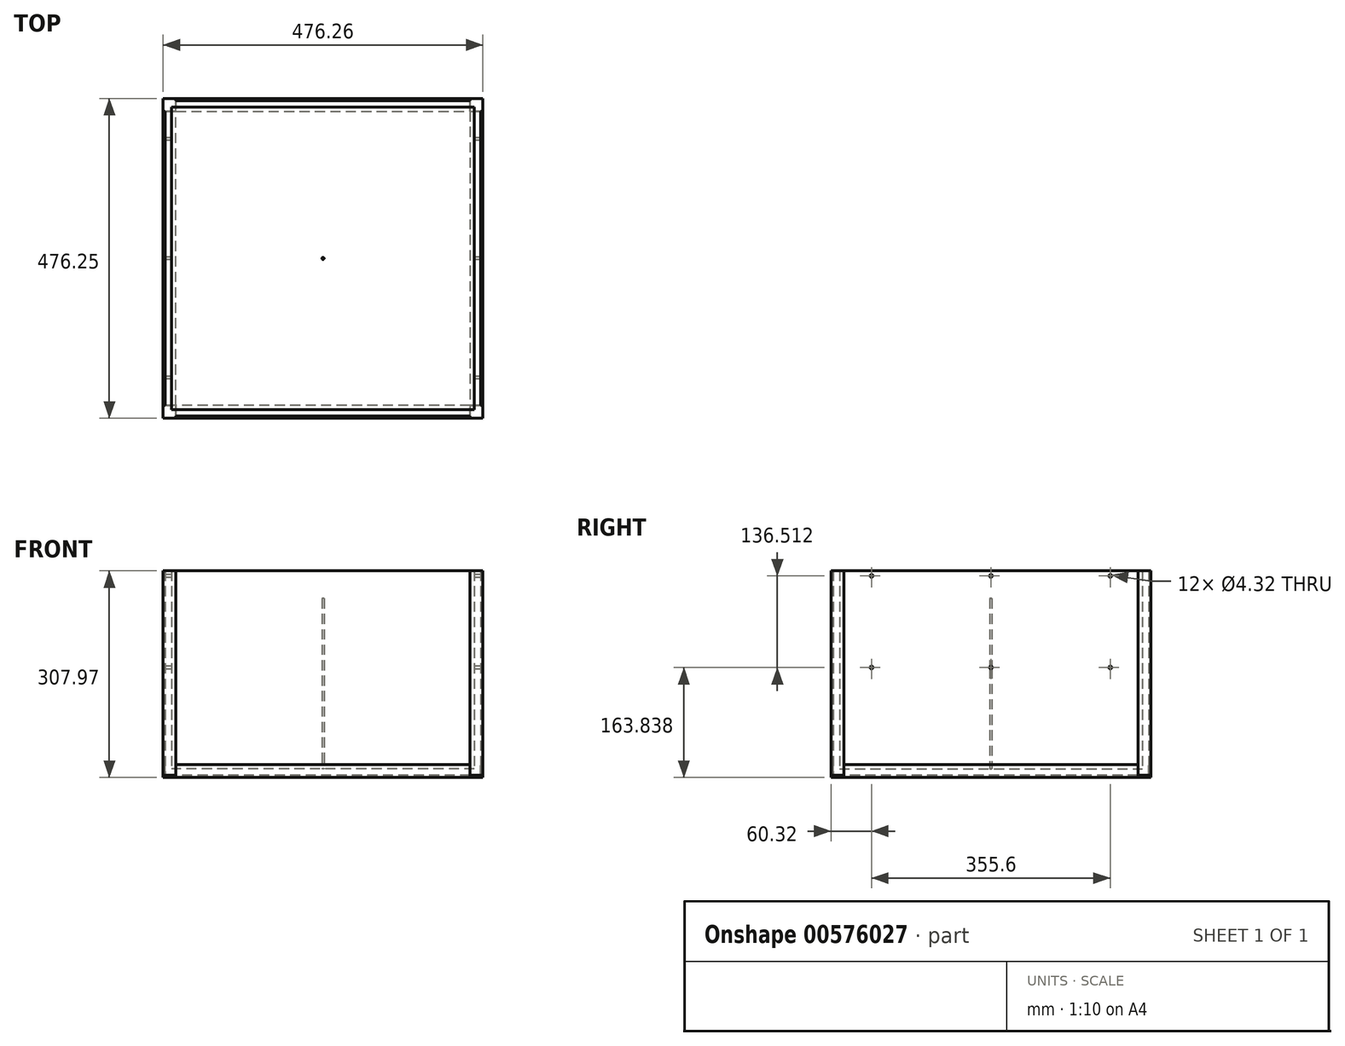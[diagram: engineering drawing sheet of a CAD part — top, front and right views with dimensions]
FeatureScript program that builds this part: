
annotation { "Feature Type Name" : "Feature", "Feature Type Description" : "" }
export const myFeature = defineFeature(function(context is Context, id is Id, definition is map)
    precondition{}
    {
        {
            var Q0;
            Q0=qCreatedBy(makeId("Top.planeOp"),FACE);
            var sketch = newSketch(context, id + "F0", { "sketchPlane" : qUnion([Q0])});
            skLineSegment(sketch, "E0.bottom", {"start": v(234.95, -234.95) * mm, "end": v(-234.95, -234.95) * mm});
            skLineSegment(sketch, "E0.top", {"start": v(234.95, 234.95) * mm, "end": v(-234.95, 234.95) * mm});
            skLineSegment(sketch, "E0.left", {"start": v(234.95, -234.95) * mm, "end": v(234.95, 234.95) * mm});
            skLineSegment(sketch, "E0.right", {"start": v(-234.95, -234.95) * mm, "end": v(-234.95, 234.95) * mm});
            skPoint(sketch, "E0.middle", {"position": v(0, 0) * mm});
            skLineSegment(sketch, "E1", {"start": v(-234.95, 238.13) * mm, "end": v(-238.13, 238.13) * mm});
            skLineSegment(sketch, "E2", {"start": v(-238.13, 238.13) * mm, "end": v(-238.13, 219.08) * mm});
            skLineSegment(sketch, "E3", {"start": v(-238.13, 219.08) * mm, "end": v(-234.95, 219.08) * mm});
            skLineSegment(sketch, "E4", {"start": v(-238.13, 238.13) * mm, "end": v(-219.08, 238.13) * mm});
            skLineSegment(sketch, "E5", {"start": v(-219.08, 238.13) * mm, "end": v(-219.08, 234.95) * mm});
            skLineSegment(sketch, "E6.1.0", {"start": v(-238.13, -238.13) * mm, "end": v(-238.13, -219.08) * mm});
            skLineSegment(sketch, "E6.1.1", {"start": v(-238.13, -238.13) * mm, "end": v(-219.08, -238.13) * mm});
            skLineSegment(sketch, "E6.1.2", {"start": v(-219.08, -238.13) * mm, "end": v(-219.08, -234.95) * mm});
            skLineSegment(sketch, "E6.1.3", {"start": v(-238.13, -219.08) * mm, "end": v(-234.95, -219.08) * mm});
            skLineSegment(sketch, "E6.1.4", {"start": v(-238.13, -234.95) * mm, "end": v(-238.13, -238.13) * mm});
            skLineSegment(sketch, "E6.2.0", {"start": v(238.13, -238.13) * mm, "end": v(219.08, -238.13) * mm});
            skLineSegment(sketch, "E6.2.1", {"start": v(238.13, -238.13) * mm, "end": v(238.13, -219.08) * mm});
            skLineSegment(sketch, "E6.2.2", {"start": v(238.13, -219.08) * mm, "end": v(234.95, -219.08) * mm});
            skLineSegment(sketch, "E6.2.3", {"start": v(219.08, -238.13) * mm, "end": v(219.08, -234.95) * mm});
            skLineSegment(sketch, "E6.2.4", {"start": v(234.95, -238.13) * mm, "end": v(238.13, -238.13) * mm});
            skLineSegment(sketch, "E6.3.0", {"start": v(238.13, 238.13) * mm, "end": v(238.13, 219.08) * mm});
            skLineSegment(sketch, "E6.3.1", {"start": v(238.13, 238.13) * mm, "end": v(219.08, 238.13) * mm});
            skLineSegment(sketch, "E6.3.2", {"start": v(219.08, 238.13) * mm, "end": v(219.08, 234.95) * mm});
            skLineSegment(sketch, "E6.3.3", {"start": v(238.13, 219.08) * mm, "end": v(234.95, 219.08) * mm});
            skLineSegment(sketch, "E6.3.4", {"start": v(238.13, 234.95) * mm, "end": v(238.13, 238.13) * mm});
            skLineSegment(sketch, "E7.0", {"start": v(225.43, 225.43) * mm, "end": v(-225.42, 225.42) * mm});
            skLineSegment(sketch, "E7.1", {"start": v(225.43, -225.42) * mm, "end": v(225.43, 225.42) * mm});
            skLineSegment(sketch, "E7.2", {"start": v(225.43, -225.42) * mm, "end": v(-225.43, -225.43) * mm});
            skLineSegment(sketch, "E7.3", {"start": v(-225.43, -225.43) * mm, "end": v(-225.42, 225.42) * mm});
            skSolve(sketch);
        }
        {
            var Q0;
            Q0 = qSketchRegion(id + "F0", true);
            extrude(context, id + "F1", {"entities" : qUnion([Q0]), "depth" : 304.8 * mm, "offsetDistance" : 25.4 * mm});
        }
        {
            var Q0;
            Q0=makeQuery(id+"F0.imprint","IMPRINT",FACE,{"disambiguationData":[TD([[makeQuery(id+"F0.imprint","IMPRINT",EDGE,{"derivedFrom":sQuery(id+"F0.wireOp",EDGE,"E7.0")}),1.0]])]});
            extrude(context, id + "F2", {"entities" : qUnion([Q0]), "operationType" : NewBodyOperationType.ADD, "depth" : 9.52 * mm, "offsetDistance" : 25.4 * mm});
        }
        {
            var Q0;
            Q0=makeQuery(id+"F1.opExtrude","SWEPT_FACE",FACE,{"disambiguationData":[OSD([sQuery(id+"F0.wireOp",EDGE,"E0.right")])]});
            var sketch = newSketch(context, id + "F3", { "sketchPlane" : qUnion([Q0])});
            skLineSegment(sketch, "E8", {"start": v(0, 304.8) * mm, "end": v(0, 297.18) * mm});
            skLineSegment(sketch, "E9", {"start": v(0, 304.8) * mm, "end": v(-177.8, 304.8) * mm});
            skLineSegment(sketch, "E10", {"start": v(-177.8, 304.8) * mm, "end": v(-177.8, 297.18) * mm});
            skLineSegment(sketch, "E11", {"start": v(0, 297.18) * mm, "end": v(0, 160.67) * mm});
            skLineSegment(sketch, "E12", {"start": v(-177.8, 297.18) * mm, "end": v(-177.8, 160.67) * mm});
            skLineSegment(sketch, "E13.MirrorCS", {"start": v(177.8, 304.8) * mm, "end": v(177.8, 297.18) * mm});
            skLineSegment(sketch, "E14.MirrorCS", {"start": v(177.8, 297.18) * mm, "end": v(177.8, 160.67) * mm});
            skLineSegment(sketch, "E15.MirrorCS", {"start": v(0, 304.8) * mm, "end": v(177.8, 304.8) * mm});
            skSolve(sketch);
        }
        {
            var Q0;
            Q0=sQuery(id+"F3.wireOp",VERTEX,"E12.start");
            var Q1;
            Q1=sQuery(id+"F3.wireOp",VERTEX,"E12.end");
            var Q2;
            Q2=sQuery(id+"F3.wireOp",VERTEX,"E8.end");
            var Q3;
            Q3=sQuery(id+"F3.wireOp",VERTEX,"E11.end");
            var Q4;
            Q4=sQuery(id+"F3.wireOp",VERTEX,"E14.MirrorCS.start");
            var Q5;
            Q5=sQuery(id+"F3.wireOp",VERTEX,"E14.MirrorCS.end");
            var Q6;
            Q6=makeQuery(id+"F1.opExtrude","SWEPT_BODY",BODY,{"disambiguationData":[OSD([sQuery(id+"F0.wireOp",EDGE,"E0.bottom"),sQuery(id+"F0.wireOp",EDGE,"E0.top"),sQuery(id+"F0.wireOp",EDGE,"E0.left"),sQuery(id+"F0.wireOp",EDGE,"E0.right"),sQuery(id+"F0.wireOp",EDGE,"E2"),sQuery(id+"F0.wireOp",EDGE,"E3"),sQuery(id+"F0.wireOp",EDGE,"E4"),sQuery(id+"F0.wireOp",EDGE,"E5"),sQuery(id+"F0.wireOp",EDGE,"E6.1.0"),sQuery(id+"F0.wireOp",EDGE,"E6.1.1"),sQuery(id+"F0.wireOp",EDGE,"E6.1.2"),sQuery(id+"F0.wireOp",EDGE,"E6.1.3"),sQuery(id+"F0.wireOp",EDGE,"E6.1.4"),sQuery(id+"F0.wireOp",EDGE,"E6.2.0"),sQuery(id+"F0.wireOp",EDGE,"E6.2.1"),sQuery(id+"F0.wireOp",EDGE,"E6.2.2"),sQuery(id+"F0.wireOp",EDGE,"E6.2.3"),sQuery(id+"F0.wireOp",EDGE,"E6.2.4"),sQuery(id+"F0.wireOp",EDGE,"E6.3.0"),sQuery(id+"F0.wireOp",EDGE,"E6.3.1"),sQuery(id+"F0.wireOp",EDGE,"E6.3.2"),sQuery(id+"F0.wireOp",EDGE,"E6.3.3"),sQuery(id+"F0.wireOp",EDGE,"E6.3.4"),sQuery(id+"F0.wireOp",EDGE,"E7.0"),sQuery(id+"F0.wireOp",EDGE,"E7.1"),sQuery(id+"F0.wireOp",EDGE,"E7.2"),sQuery(id+"F0.wireOp",EDGE,"E7.3")])]});
            hole(context, id + "F4", {"style" : HoleStyle.SIMPLE, "endStyle" : HoleEndStyle.BLIND, "standardTappedOrClearance" : lookupTablePath({ "standard" : "ANSI", "fit" : "Close", "size" : "#8", "type" : "Clearance" }), "standardBlindInLast" : lookupTablePath({ "fit" : "Close", "standard" : "ANSI", "size" : "#8", "type" : "Clearance" }), "holeDiameter" : 4.32 * mm, "holeDepth" : 762 * mm, "isTappedThrough" : true, "tappedDepth" : 12.7 * mm, "tapClearance" : 3, "locations" : qUnion([Q0, Q1, Q2, Q3, Q4, Q5]), "scope" : qUnion([Q6])});
        }
        {
            var Q0;
            Q0=makeQuery(id+"F1.opExtrude","SWEPT_FACE",FACE,{"disambiguationData":[OSD([sQuery(id+"F0.wireOp",EDGE,"E6.1.2")])]});
            var sketch = newSketch(context, id + "F5", { "sketchPlane" : qUnion([Q0])});
            skLineSegment(sketch, "E16", {"start": v(-238.12, -3.17) * mm, "end": v(-238.12, 15.87) * mm});
            skLineSegment(sketch, "E17", {"start": v(-238.12, 15.87) * mm, "end": v(-234.95, 15.87) * mm});
            skLineSegment(sketch, "E18", {"start": v(-234.95, 15.87) * mm, "end": v(-234.95, 0) * mm});
            skLineSegment(sketch, "E19", {"start": v(-234.95, 0) * mm, "end": v(-219.07, 0) * mm});
            skLineSegment(sketch, "E20", {"start": v(-219.07, 0) * mm, "end": v(-219.07, -3.17) * mm});
            skLineSegment(sketch, "E21", {"start": v(-219.07, -3.17) * mm, "end": v(-238.12, -3.17) * mm});
            skSolve(sketch);
        }
        {
            var Q0;
            Q0 = qSketchRegion(id + "F5", true);
            var Q1;
            Q1=makeQuery(id+"F1.opExtrude","SWEPT_FACE",FACE,{"disambiguationData":[OSD([sQuery(id+"F0.wireOp",EDGE,"E6.2.3")])]});
            extrude(context, id + "F6", {"entities" : qUnion([Q0]), "endBound" : BoundingType.UP_TO_SURFACE, "depth" : 25.4 * mm, "endBoundEntityFace" : qUnion([Q1]), "offsetDistance" : 25.4 * mm});
        }
        {
            var Q0;
            Q0=makeQuery(id+"F2.opExtrude","CAP_FACE",FACE,{"disambiguationData":[OSD([sQuery(id+"F0.wireOp",EDGE,"E7.0"),sQuery(id+"F0.wireOp",EDGE,"E7.1"),sQuery(id+"F0.wireOp",EDGE,"E7.2"),sQuery(id+"F0.wireOp",EDGE,"E7.3")])],"isStart":false});
            var sketch = newSketch(context, id + "F7", { "sketchPlane" : qUnion([Q0])});
            skCircle(sketch, "E22", {"center": v(0, 0) * mm, "radius": 1.59 * mm});
            skSolve(sketch);
        }
        {
            var Q0;
            Q0 = qSketchRegion(id + "F7", true);
            extrude(context, id + "F8", {"entities" : qUnion([Q0]), "operationType" : NewBodyOperationType.ADD, "depth" : 254 * mm, "offsetDistance" : 25.4 * mm});
        }
        {
            var Q0;
            Q0=makeQuery(id+"F6.opExtrude","SWEPT_BODY",BODY,{"disambiguationData":[OSD([sQuery(id+"F5.wireOp",EDGE,"E16"),sQuery(id+"F5.wireOp",EDGE,"E17"),sQuery(id+"F5.wireOp",EDGE,"E18"),sQuery(id+"F5.wireOp",EDGE,"E19"),sQuery(id+"F5.wireOp",EDGE,"E20"),sQuery(id+"F5.wireOp",EDGE,"E21")])]});
            var Q1;
            Q1=makeQuery(id+"F8.opExtrude","SWEPT_FACE",FACE,{"disambiguationData":[OSD([sQuery(id+"F7.wireOp",EDGE,"E22")])]});
            circularPattern(context, id + "F9", {"entities" : qUnion([Q0]), "axis" : qUnion([Q1]), "angle" : 360 * degree, "instanceCount" : 4, "equalSpace" : true});
        }
    });
